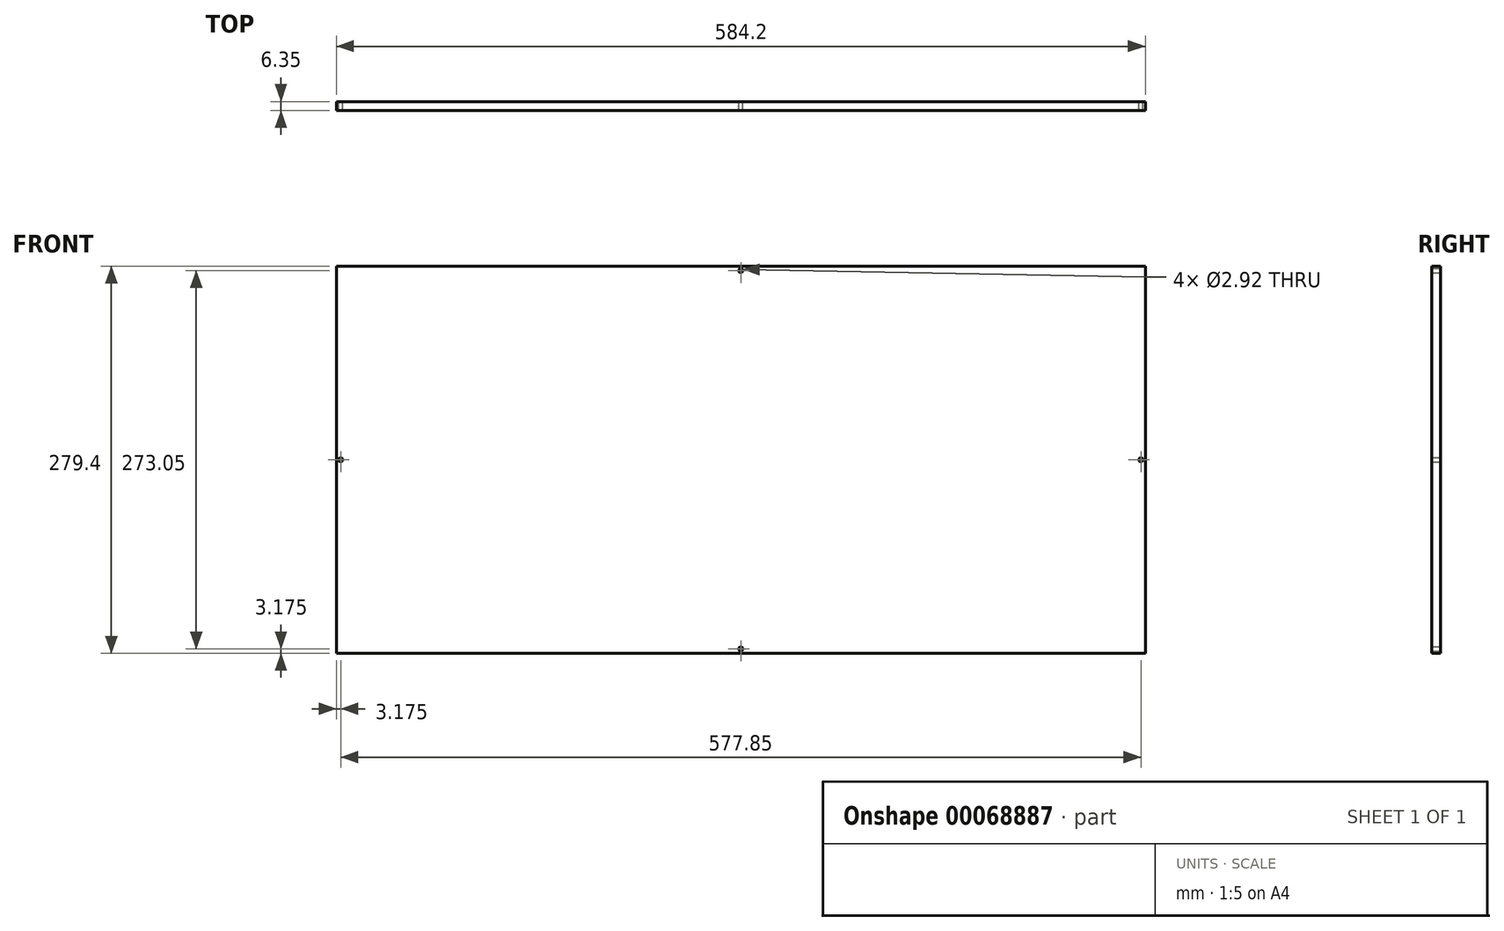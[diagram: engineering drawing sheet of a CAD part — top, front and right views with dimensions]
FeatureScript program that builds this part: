
annotation { "Feature Type Name" : "Feature", "Feature Type Description" : "" }
export const myFeature = defineFeature(function(context is Context, id is Id, definition is map)
    precondition{}
    {
        {
            var Q0;
            Q0=qCreatedBy(makeId("Front.planeOp"),FACE);
            var sketch = newSketch(context, id + "F0", { "sketchPlane" : qUnion([Q0])});
            skLineSegment(sketch, "E0.rect.bottom", {"start": v(292.1, -139.7) * mm, "end": v(-292.1, -139.7) * mm});
            skLineSegment(sketch, "E0.rect.top", {"start": v(292.1, 139.7) * mm, "end": v(-292.1, 139.7) * mm});
            skLineSegment(sketch, "E0.rect.left", {"start": v(292.1, -139.7) * mm, "end": v(292.1, 139.7) * mm});
            skLineSegment(sketch, "E0.rect.right", {"start": v(-292.1, -139.7) * mm, "end": v(-292.1, 139.7) * mm});
            skPoint(sketch, "E0.rect.middle", {"position": v(0, 0) * mm});
            skLineSegment(sketch, "E1", {"start": v(-288.93, 139.7) * mm, "end": v(-288.93, -139.7) * mm, "construction": true});
            skLineSegment(sketch, "E2", {"start": v(288.93, 139.7) * mm, "end": v(288.93, -139.7) * mm, "construction": true});
            skLineSegment(sketch, "E3", {"start": v(0, 139.7) * mm, "end": v(0, -139.7) * mm, "construction": true});
            skLineSegment(sketch, "E4.0", {"start": v(292.1, -136.53) * mm, "end": v(-292.1, -136.52) * mm, "construction": true});
            skLineSegment(sketch, "E5.0", {"start": v(317.5, 136.52) * mm, "end": v(-317.5, 136.53) * mm, "construction": true});
            skLineSegment(sketch, "E6", {"start": v(-292.1, 0) * mm, "end": v(292.1, 0) * mm, "construction": true});
            skCircle(sketch, "E7", {"center": v(0, 136.53) * mm, "radius": 1.46 * mm});
            skCircle(sketch, "E8", {"center": v(288.93, 0) * mm, "radius": 1.46 * mm});
            skCircle(sketch, "E9", {"center": v(0, -136.53) * mm, "radius": 1.46 * mm});
            skCircle(sketch, "E10", {"center": v(-288.93, 0) * mm, "radius": 1.46 * mm});
            skSolve(sketch);
        }
        {
            var Q0;
            Q0=makeQuery(id+"F0.imprint","IMPRINT",FACE,{"disambiguationData":[TD([[makeQuery(id+"F0.imprint","IMPRINT",EDGE,{"derivedFrom":sQuery(id+"F0.wireOp",EDGE,"E0.rect.bottom")}),-1.0]])]});
            extrude(context, id + "F1", {"entities" : qUnion([Q0]), "depth" : 6.35 * mm});
        }
    });
